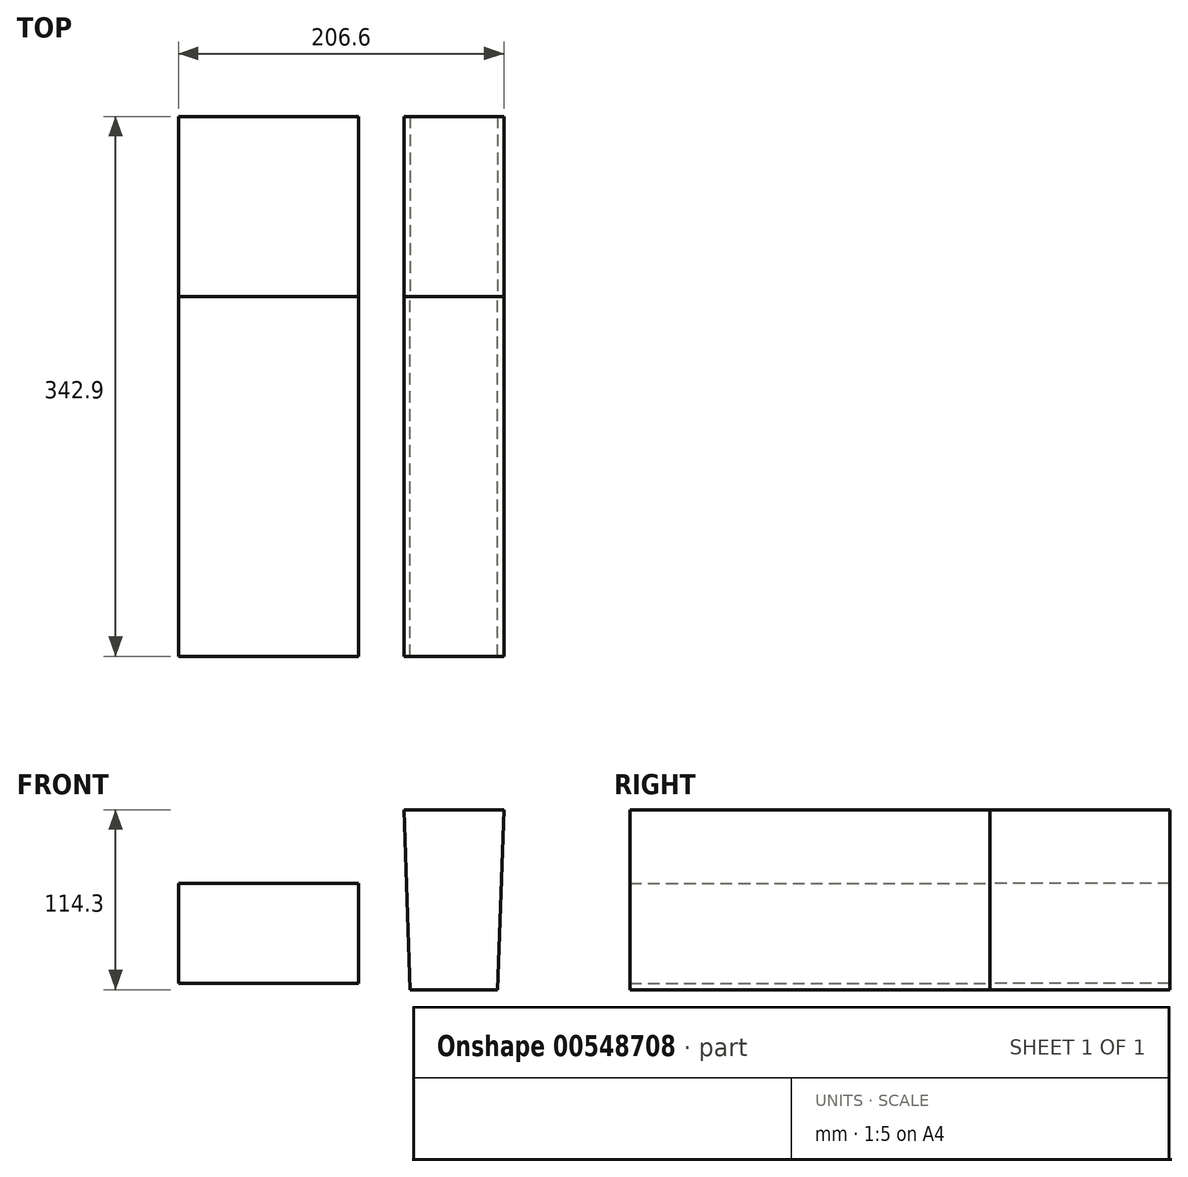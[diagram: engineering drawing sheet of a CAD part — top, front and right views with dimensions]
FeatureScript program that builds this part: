
annotation { "Feature Type Name" : "Feature", "Feature Type Description" : "" }
export const myFeature = defineFeature(function(context is Context, id is Id, definition is map)
    precondition{}
    {
        {
            var Q0;
            Q0=qCreatedBy(makeId("Front.planeOp"),FACE);
            var sketch = newSketch(context, id + "F0", { "sketchPlane" : qUnion([Q0])});
            skLineSegment(sketch, "E0", {"start": v(-45.9, 57.14) * mm, "end": v(17.6, 57.14) * mm});
            skLineSegment(sketch, "E1", {"start": v(17.6, 57.14) * mm, "end": v(13.6, -57.16) * mm});
            skLineSegment(sketch, "E2", {"start": v(13.6, -57.16) * mm, "end": v(-41.92, -57.16) * mm});
            skLineSegment(sketch, "E3", {"start": v(-41.92, -57.16) * mm, "end": v(-45.9, 57.14) * mm});
            skPoint(sketch, "E4", {"position": v(-14.16, -57.16) * mm});
            skPoint(sketch, "E5", {"position": v(-14.16, 57.14) * mm});
            skLineSegment(sketch, "E6", {"start": v(-14.16, 57.14) * mm, "end": v(-14.16, -57.16) * mm});
            skSolve(sketch);
        }
        {
            var Q0;
            Q0 = qSketchRegion(id + "F0", true);
            extrude(context, id + "F1", {"entities" : qUnion([Q0]), "depth" : 228.6 * mm, "offsetDistance" : 25.4 * mm});
        }
        {
            var Q0;
            Q0=qCreatedBy(makeId("Front.planeOp"),FACE);
            var sketch = newSketch(context, id + "F2", { "sketchPlane" : qUnion([Q0])});
            skLineSegment(sketch, "E7.bottom", {"start": v(-189, 10.27) * mm, "end": v(-74.7, 10.27) * mm});
            skLineSegment(sketch, "E7.top", {"start": v(-189, -53.23) * mm, "end": v(-74.7, -53.23) * mm});
            skLineSegment(sketch, "E7.left", {"start": v(-189, 10.27) * mm, "end": v(-189, -53.23) * mm});
            skLineSegment(sketch, "E7.right", {"start": v(-74.7, 10.27) * mm, "end": v(-74.7, -53.23) * mm});
            skSolve(sketch);
        }
        {
            var Q0;
            Q0 = qSketchRegion(id + "F2", true);
            extrude(context, id + "F3", {"entities" : qUnion([Q0]), "depth" : 228.6 * mm, "offsetDistance" : 25.4 * mm});
        }
        {
            var Q0;
            Q0 = qSketchRegion(id + "F0", true);
            extrude(context, id + "F4", {"entities" : qUnion([Q0]), "oppositeDirection" : true, "depth" : 114.3 * mm, "offsetDistance" : 25.4 * mm});
        }
        {
            var Q0;
            Q0 = qSketchRegion(id + "F2", true);
            extrude(context, id + "F5", {"entities" : qUnion([Q0]), "oppositeDirection" : true, "depth" : 114.3 * mm, "hasOffset" : true, "offsetDistance" : 114.3 * mm, "offsetOppositeDirection" : true});
        }
    });
